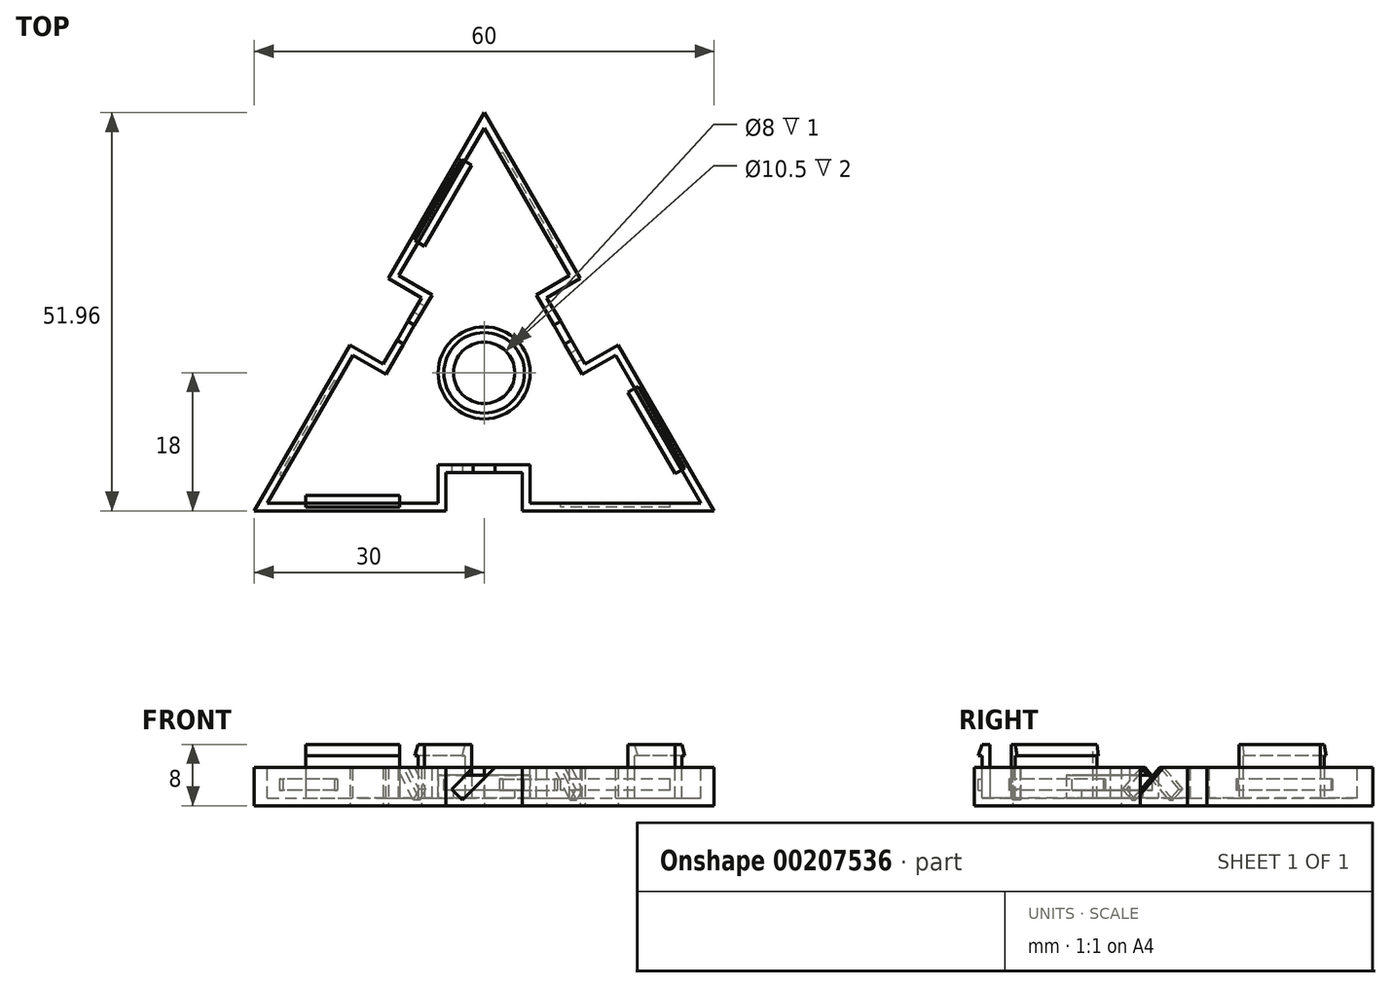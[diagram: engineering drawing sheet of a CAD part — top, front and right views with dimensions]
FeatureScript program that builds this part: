
annotation { "Feature Type Name" : "Feature", "Feature Type Description" : "" }
export const myFeature = defineFeature(function(context is Context, id is Id, definition is map)
    precondition{}
    {
        {
            var Q0;
            Q0=qCreatedBy(makeId("Top.planeOp"),FACE);
            var sketch = newSketch(context, id + "F0", { "sketchPlane" : qUnion([Q0])});
            skLineSegment(sketch, "E0", {"start": v(0, 0) * mm, "end": v(60, 0) * mm});
            skLineSegment(sketch, "E1", {"start": v(0, 0) * mm, "end": v(30, 51.96) * mm});
            skLineSegment(sketch, "E2", {"start": v(30, 51.96) * mm, "end": v(60, 0) * mm});
            skSolve(sketch);
        }
        {
            var Q0;
            Q0=makeQuery(id+"F0.imprint","IMPRINT",FACE,{"disambiguationData":[TD([[makeQuery(id+"F0.imprint","IMPRINT",EDGE,{"derivedFrom":sQuery(id+"F0.wireOp",EDGE,"E0")}),1.0]])]});
            extrude(context, id + "F1", {"entities" : qUnion([Q0]), "depth" : 10 * mm});
        }
        {
            var Q0;
            Q0=makeQuery(id+"F1.opExtrude","SWEPT_FACE",FACE,{"disambiguationData":[OSD([sQuery(id+"F0.wireOp",EDGE,"E0")])]});
            var sketch = newSketch(context, id + "F2", { "sketchPlane" : qUnion([Q0])});
            skLineSegment(sketch, "E3.bottom", {"start": v(25, 10) * mm, "end": v(35, 10) * mm});
            skLineSegment(sketch, "E3.top", {"start": v(25, 0) * mm, "end": v(35, 0) * mm});
            skLineSegment(sketch, "E3.left", {"start": v(25, 10) * mm, "end": v(25, 0) * mm});
            skLineSegment(sketch, "E3.right", {"start": v(35, 10) * mm, "end": v(35, 0) * mm});
            skSolve(sketch);
        }
        {
            var Q0;
            Q0=makeQuery(id+"F2.imprint","IMPRINT",FACE,{"disambiguationData":[TD([[makeQuery(id+"F2.imprint","IMPRINT",EDGE,{"derivedFrom":sQuery(id+"F2.wireOp",EDGE,"E3.bottom")}),-1.0]])]});
            extrude(context, id + "F3", {"entities" : qUnion([Q0]), "operationType" : NewBodyOperationType.REMOVE, "oppositeDirection" : true, "depth" : 5 * mm});
        }
        {
            var Q0;
            Q0=makeQuery(id+"F1.opExtrude","SWEPT_FACE",FACE,{"disambiguationData":[OSD([sQuery(id+"F0.wireOp",EDGE,"E1")])]});
            var sketch = newSketch(context, id + "F4", { "sketchPlane" : qUnion([Q0])});
            skLineSegment(sketch, "E4.bottom", {"start": v(-35, 10) * mm, "end": v(-25, 10) * mm});
            skLineSegment(sketch, "E4.top", {"start": v(-35, 0) * mm, "end": v(-25, 0) * mm});
            skLineSegment(sketch, "E4.left", {"start": v(-35, 10) * mm, "end": v(-35, 0) * mm});
            skLineSegment(sketch, "E4.right", {"start": v(-25, 10) * mm, "end": v(-25, 0) * mm});
            skSolve(sketch);
        }
        {
            var Q0;
            Q0=makeQuery(id+"F4.imprint","IMPRINT",FACE,{"disambiguationData":[TD([[makeQuery(id+"F4.imprint","IMPRINT",EDGE,{"derivedFrom":sQuery(id+"F4.wireOp",EDGE,"E4.bottom")}),1.0]])]});
            extrude(context, id + "F5", {"entities" : qUnion([Q0]), "operationType" : NewBodyOperationType.REMOVE, "oppositeDirection" : true, "depth" : 5 * mm});
        }
        {
            var Q0;
            Q0=makeQuery(id+"F1.opExtrude","SWEPT_FACE",FACE,{"disambiguationData":[OSD([sQuery(id+"F0.wireOp",EDGE,"E2")])]});
            var sketch = newSketch(context, id + "F6", { "sketchPlane" : qUnion([Q0])});
            skLineSegment(sketch, "E5.bottom", {"start": v(-5, 10) * mm, "end": v(5, 10) * mm});
            skLineSegment(sketch, "E5.top", {"start": v(-5, 0) * mm, "end": v(5, 0) * mm});
            skLineSegment(sketch, "E5.left", {"start": v(-5, 10) * mm, "end": v(-5, 0) * mm});
            skLineSegment(sketch, "E5.right", {"start": v(5, 10) * mm, "end": v(5, 0) * mm});
            skSolve(sketch);
        }
        {
            var Q0;
            Q0=makeQuery(id+"F6.imprint","IMPRINT",FACE,{"disambiguationData":[TD([[makeQuery(id+"F6.imprint","IMPRINT",EDGE,{"derivedFrom":sQuery(id+"F6.wireOp",EDGE,"E5.bottom")}),1.0]])]});
            extrude(context, id + "F7", {"entities" : qUnion([Q0]), "operationType" : NewBodyOperationType.REMOVE, "oppositeDirection" : true, "depth" : 5 * mm});
        }
        {
            var Q0;
            Q0=makeQuery(id+"F1.opExtrude","CAP_FACE",FACE,{"disambiguationData":[OSD([sQuery(id+"F0.wireOp",EDGE,"E0"),sQuery(id+"F0.wireOp",EDGE,"E1"),sQuery(id+"F0.wireOp",EDGE,"E2")])],"isStart":false});
            var sketch = newSketch(context, id + "F8", { "sketchPlane" : qUnion([Q0])});
            skLineSegment(sketch, "E6.0", {"start": v(23.2, 28.18) * mm, "end": v(18.87, 30.68) * mm});
            skLineSegment(sketch, "E6.1", {"start": v(17.2, 17.78) * mm, "end": v(23.2, 28.18) * mm});
            skLineSegment(sketch, "E6.2", {"start": v(17.2, 17.78) * mm, "end": v(12.87, 20.28) * mm});
            skLineSegment(sketch, "E6.3", {"start": v(1.73, 1) * mm, "end": v(12.87, 20.28) * mm});
            skLineSegment(sketch, "E6.4", {"start": v(42.8, 17.78) * mm, "end": v(47.13, 20.28) * mm});
            skLineSegment(sketch, "E6.5", {"start": v(36.8, 28.18) * mm, "end": v(42.8, 17.78) * mm});
            skLineSegment(sketch, "E6.6", {"start": v(36.8, 28.18) * mm, "end": v(41.13, 30.68) * mm});
            skLineSegment(sketch, "E6.7", {"start": v(30, 49.96) * mm, "end": v(41.13, 30.68) * mm});
            skLineSegment(sketch, "E6.8", {"start": v(47.13, 20.28) * mm, "end": v(58.27, 1) * mm});
            skLineSegment(sketch, "E6.9", {"start": v(36, 1) * mm, "end": v(58.27, 1) * mm});
            skLineSegment(sketch, "E6.10", {"start": v(36, 6) * mm, "end": v(36, 1) * mm});
            skLineSegment(sketch, "E6.11", {"start": v(24, 6) * mm, "end": v(36, 6) * mm});
            skLineSegment(sketch, "E6.12", {"start": v(18.87, 30.68) * mm, "end": v(30, 49.96) * mm});
            skLineSegment(sketch, "E6.13", {"start": v(24, 6) * mm, "end": v(24, 1) * mm});
            skLineSegment(sketch, "E6.14", {"start": v(1.73, 1) * mm, "end": v(24, 1) * mm});
            skSolve(sketch);
        }
        {
            var Q0;
            Q0=makeQuery(id+"F8.imprint","IMPRINT",FACE,{"disambiguationData":[TD([[makeQuery(id+"F8.imprint","IMPRINT",EDGE,{"derivedFrom":sQuery(id+"F8.wireOp",EDGE,"E6.0")}),-1.0]])]});
            extrude(context, id + "F9", {"entities" : qUnion([Q0]), "operationType" : NewBodyOperationType.REMOVE, "oppositeDirection" : true, "depth" : 9 * mm});
        }
        {
            var Q0;
            Q0=makeQuery(id+"F1.opExtrude","CAP_FACE",FACE,{"disambiguationData":[OSD([sQuery(id+"F0.wireOp",EDGE,"E0"),sQuery(id+"F0.wireOp",EDGE,"E1"),sQuery(id+"F0.wireOp",EDGE,"E2")])],"isStart":false});
            extrude(context, id + "F10", {"entities" : qUnion([Q0]), "operationType" : NewBodyOperationType.REMOVE, "oppositeDirection" : true, "depth" : 5 * mm});
        }
        {
            var Q0;
            Q0=makeQuery(id+"F9.boolean.opBoolean","COPY",FACE,{"derivedFrom":makeQuery(id+"F9.opExtrude","SWEPT_FACE",FACE,{"disambiguationData":[OSD([sQuery(id+"F8.wireOp",EDGE,"E6.12")])]})});
            var sketch = newSketch(context, id + "F11", { "sketchPlane" : qUnion([Q0])});
            skLineSegment(sketch, "E7.bottom", {"start": v(41, 8) * mm, "end": v(53.27, 8) * mm});
            skLineSegment(sketch, "E7.top", {"start": v(41, 1) * mm, "end": v(53.27, 1) * mm});
            skLineSegment(sketch, "E7.left", {"start": v(41, 8) * mm, "end": v(41, 1) * mm});
            skLineSegment(sketch, "E7.right", {"start": v(53.27, 8) * mm, "end": v(53.27, 1) * mm});
            skSolve(sketch);
        }
        {
            var Q0;
            {var subQ0=sQuery(id+"F11.wireOp",EDGE,"E7.top");Q0=makeQuery(id+"F11.imprint","IMPRINT",FACE,{"disambiguationData":[TD([[makeQuery(id+"F11.imprint","IMPRINT",EDGE,{"derivedFrom":subQ0}),1.0]])]});}
            var Q1;
            {var subQ0=sQuery(id+"F11.wireOp",EDGE,"E7.bottom");Q1=makeQuery(id+"F11.imprint","IMPRINT",FACE,{"disambiguationData":[TD([[makeQuery(id+"F11.imprint","IMPRINT",EDGE,{"derivedFrom":subQ0}),-1.0]])]});}
            extrude(context, id + "F12", {"entities" : qUnion([Q0, Q1]), "operationType" : NewBodyOperationType.ADD, "depth" : 1 * mm});
        }
        {
            var Q0;
            Q0=makeQuery(id+"F9.boolean.opBoolean","COPY",FACE,{"derivedFrom":makeQuery(id+"F9.opExtrude","SWEPT_FACE",FACE,{"disambiguationData":[OSD([sQuery(id+"F8.wireOp",EDGE,"E6.14")])]})});
            var sketch = newSketch(context, id + "F13", { "sketchPlane" : qUnion([Q0])});
            skLineSegment(sketch, "E8.bottom", {"start": v(-19, 8) * mm, "end": v(-6.73, 8) * mm});
            skLineSegment(sketch, "E8.top", {"start": v(-19, 1) * mm, "end": v(-6.73, 1) * mm});
            skLineSegment(sketch, "E8.left", {"start": v(-19, 8) * mm, "end": v(-19, 1) * mm});
            skLineSegment(sketch, "E8.right", {"start": v(-6.73, 8) * mm, "end": v(-6.73, 1) * mm});
            skSolve(sketch);
        }
        {
            var Q0;
            {var subQ0=sQuery(id+"F13.wireOp",EDGE,"E8.top");Q0=makeQuery(id+"F13.imprint","IMPRINT",FACE,{"disambiguationData":[TD([[makeQuery(id+"F13.imprint","IMPRINT",EDGE,{"derivedFrom":subQ0}),-1.0]])]});}
            var Q1;
            {var subQ0=sQuery(id+"F13.wireOp",EDGE,"E8.bottom");Q1=makeQuery(id+"F13.imprint","IMPRINT",FACE,{"disambiguationData":[TD([[makeQuery(id+"F13.imprint","IMPRINT",EDGE,{"derivedFrom":subQ0}),-1.0]])]});}
            extrude(context, id + "F14", {"entities" : qUnion([Q0, Q1]), "operationType" : NewBodyOperationType.ADD, "depth" : 1 * mm});
        }
        {
            var Q0;
            Q0=makeQuery(id+"F9.boolean.opBoolean","COPY",FACE,{"derivedFrom":makeQuery(id+"F9.opExtrude","SWEPT_FACE",FACE,{"disambiguationData":[OSD([sQuery(id+"F8.wireOp",EDGE,"E6.8")])]})});
            var sketch = newSketch(context, id + "F15", { "sketchPlane" : qUnion([Q0])});
            skLineSegment(sketch, "E9.bottom", {"start": v(11, 1) * mm, "end": v(23.27, 1) * mm});
            skLineSegment(sketch, "E9.top", {"start": v(11, 8) * mm, "end": v(23.27, 8) * mm});
            skLineSegment(sketch, "E9.left", {"start": v(11, 1) * mm, "end": v(11, 8) * mm});
            skLineSegment(sketch, "E9.right", {"start": v(23.27, 1) * mm, "end": v(23.27, 8) * mm});
            skSolve(sketch);
        }
        {
            var Q0;
            {var subQ0=sQuery(id+"F15.wireOp",EDGE,"E9.bottom");Q0=makeQuery(id+"F15.imprint","IMPRINT",FACE,{"disambiguationData":[TD([[makeQuery(id+"F15.imprint","IMPRINT",EDGE,{"derivedFrom":subQ0}),1.0]])]});}
            var Q1;
            {var subQ0=sQuery(id+"F15.wireOp",EDGE,"E9.top");Q1=makeQuery(id+"F15.imprint","IMPRINT",FACE,{"disambiguationData":[TD([[makeQuery(id+"F15.imprint","IMPRINT",EDGE,{"derivedFrom":subQ0}),-1.0]])]});}
            extrude(context, id + "F16", {"entities" : qUnion([Q0, Q1]), "operationType" : NewBodyOperationType.ADD, "depth" : 1 * mm});
        }
        {
            var Q0;
            Q0=makeQuery(id+"F14.opExtrude","CAP_FACE",FACE,{"disambiguationData":[OSD([sQuery(id+"F13.wireOp",EDGE,"E8.bottom"),sQuery(id+"F13.wireOp",EDGE,"E8.top"),sQuery(id+"F13.wireOp",EDGE,"E8.left"),sQuery(id+"F13.wireOp",EDGE,"E8.right")])],"isStart":true});
            var sketch = newSketch(context, id + "F17", { "sketchPlane" : qUnion([Q0])});
            skLineSegment(sketch, "E10.bottom", {"start": v(6.73, 8) * mm, "end": v(19, 8) * mm});
            skLineSegment(sketch, "E10.top", {"start": v(6.73, 6.5) * mm, "end": v(19, 6.5) * mm});
            skLineSegment(sketch, "E10.left", {"start": v(6.73, 8) * mm, "end": v(6.73, 6.5) * mm});
            skLineSegment(sketch, "E10.right", {"start": v(19, 8) * mm, "end": v(19, 6.5) * mm});
            skSolve(sketch);
        }
        {
            var Q0;
            Q0=makeQuery(id+"F17.imprint","IMPRINT",FACE,{"disambiguationData":[TD([[makeQuery(id+"F17.imprint","IMPRINT",EDGE,{"derivedFrom":sQuery(id+"F17.wireOp",EDGE,"E10.bottom")}),1.0]])]});
            extrude(context, id + "F18", {"entities" : qUnion([Q0]), "operationType" : NewBodyOperationType.ADD, "depth" : 0.5 * mm});
        }
        {
            var Q0;
            Q0=makeQuery(id+"F18.opExtrude","CAP_EDGE",EDGE,{"disambiguationData":[OSD([sQuery(id+"F17.wireOp",EDGE,"E10.bottom")])],"isStart":false});
            chamfer(context, id + "F19", {"entities" : qUnion([Q0]), "chamferType" : ChamferType.TWO_OFFSETS, "width1" : 0.5 * mm, "oppositeDirection" : true, "width2" : 1.5 * mm, "tangentPropagation" : true});
        }
        {
            var Q0;
            Q0=makeQuery(id+"F16.opExtrude","CAP_FACE",FACE,{"disambiguationData":[OSD([sQuery(id+"F15.wireOp",EDGE,"E9.bottom"),sQuery(id+"F15.wireOp",EDGE,"E9.top"),sQuery(id+"F15.wireOp",EDGE,"E9.left"),sQuery(id+"F15.wireOp",EDGE,"E9.right")])],"isStart":true});
            var sketch = newSketch(context, id + "F20", { "sketchPlane" : qUnion([Q0])});
            skLineSegment(sketch, "E11.bottom", {"start": v(-23.27, 8) * mm, "end": v(-11, 8) * mm});
            skLineSegment(sketch, "E11.top", {"start": v(-23.27, 6.5) * mm, "end": v(-11, 6.5) * mm});
            skLineSegment(sketch, "E11.left", {"start": v(-23.27, 8) * mm, "end": v(-23.27, 6.5) * mm});
            skLineSegment(sketch, "E11.right", {"start": v(-11, 8) * mm, "end": v(-11, 6.5) * mm});
            skSolve(sketch);
        }
        {
            var Q0;
            Q0=makeQuery(id+"F20.imprint","IMPRINT",FACE,{"disambiguationData":[TD([[makeQuery(id+"F20.imprint","IMPRINT",EDGE,{"derivedFrom":sQuery(id+"F20.wireOp",EDGE,"E11.bottom")}),1.0]])]});
            extrude(context, id + "F21", {"entities" : qUnion([Q0]), "operationType" : NewBodyOperationType.ADD, "depth" : 0.5 * mm});
        }
        {
            var Q0;
            Q0=makeQuery(id+"F21.opExtrude","CAP_EDGE",EDGE,{"disambiguationData":[OSD([sQuery(id+"F20.wireOp",EDGE,"E11.bottom")])],"isStart":false});
            chamfer(context, id + "F22", {"entities" : qUnion([Q0]), "chamferType" : ChamferType.TWO_OFFSETS, "width1" : 0.5 * mm, "oppositeDirection" : true, "width2" : 1.5 * mm, "tangentPropagation" : true});
        }
        {
            var Q0;
            Q0=makeQuery(id+"F12.opExtrude","CAP_FACE",FACE,{"disambiguationData":[OSD([sQuery(id+"F11.wireOp",EDGE,"E7.bottom"),sQuery(id+"F11.wireOp",EDGE,"E7.top"),sQuery(id+"F11.wireOp",EDGE,"E7.left"),sQuery(id+"F11.wireOp",EDGE,"E7.right")])],"isStart":true});
            var sketch = newSketch(context, id + "F23", { "sketchPlane" : qUnion([Q0])});
            skLineSegment(sketch, "E12.bottom", {"start": v(-53.27, 8) * mm, "end": v(-41, 8) * mm});
            skLineSegment(sketch, "E12.top", {"start": v(-53.27, 6.5) * mm, "end": v(-41, 6.5) * mm});
            skLineSegment(sketch, "E12.left", {"start": v(-53.27, 8) * mm, "end": v(-53.27, 6.5) * mm});
            skLineSegment(sketch, "E12.right", {"start": v(-41, 8) * mm, "end": v(-41, 6.5) * mm});
            skSolve(sketch);
        }
        {
            var Q0;
            Q0=makeQuery(id+"F23.imprint","IMPRINT",FACE,{"disambiguationData":[TD([[makeQuery(id+"F23.imprint","IMPRINT",EDGE,{"derivedFrom":sQuery(id+"F23.wireOp",EDGE,"E12.bottom")}),1.0]])]});
            extrude(context, id + "F24", {"entities" : qUnion([Q0]), "operationType" : NewBodyOperationType.ADD, "depth" : 0.5 * mm});
        }
        {
            var Q0;
            Q0=makeQuery(id+"F24.opExtrude","CAP_EDGE",EDGE,{"disambiguationData":[OSD([sQuery(id+"F23.wireOp",EDGE,"E12.bottom")])],"isStart":false});
            chamfer(context, id + "F25", {"entities" : qUnion([Q0]), "chamferType" : ChamferType.TWO_OFFSETS, "width1" : 0.5 * mm, "oppositeDirection" : true, "width2" : 1.5 * mm, "tangentPropagation" : true});
        }
        {
            var Q0;
            Q0=makeQuery(id+"F9.boolean.opBoolean","COPY",FACE,{"derivedFrom":makeQuery(id+"F9.opExtrude","SWEPT_FACE",FACE,{"disambiguationData":[OSD([sQuery(id+"F8.wireOp",EDGE,"E6.7")])]})});
            var sketch = newSketch(context, id + "F26", { "sketchPlane" : qUnion([Q0])});
            skLineSegment(sketch, "E13.bottom", {"start": v(-24.27, 3.5) * mm, "end": v(-10, 3.5) * mm});
            skLineSegment(sketch, "E13.top", {"start": v(-24.27, 2) * mm, "end": v(-10, 2) * mm});
            skLineSegment(sketch, "E13.left", {"start": v(-24.27, 3.5) * mm, "end": v(-24.27, 2) * mm});
            skLineSegment(sketch, "E13.right", {"start": v(-10, 3.5) * mm, "end": v(-10, 2) * mm});
            skSolve(sketch);
        }
        {
            var Q0;
            Q0=makeQuery(id+"F26.imprint","IMPRINT",FACE,{"disambiguationData":[TD([[makeQuery(id+"F26.imprint","IMPRINT",EDGE,{"derivedFrom":sQuery(id+"F26.wireOp",EDGE,"E13.bottom")}),-1.0]])]});
            extrude(context, id + "F27", {"entities" : qUnion([Q0]), "operationType" : NewBodyOperationType.REMOVE, "oppositeDirection" : true, "depth" : 0.5 * mm});
        }
        {
            var Q0;
            Q0=makeQuery(id+"F9.boolean.opBoolean","COPY",FACE,{"derivedFrom":makeQuery(id+"F9.opExtrude","SWEPT_FACE",FACE,{"disambiguationData":[OSD([sQuery(id+"F8.wireOp",EDGE,"E6.9")])]})});
            var sketch = newSketch(context, id + "F28", { "sketchPlane" : qUnion([Q0])});
            skLineSegment(sketch, "E14.bottom", {"start": v(-54.27, 2) * mm, "end": v(-40, 2) * mm});
            skLineSegment(sketch, "E14.top", {"start": v(-54.27, 3.5) * mm, "end": v(-40, 3.5) * mm});
            skLineSegment(sketch, "E14.left", {"start": v(-54.27, 2) * mm, "end": v(-54.27, 3.5) * mm});
            skLineSegment(sketch, "E14.right", {"start": v(-40, 2) * mm, "end": v(-40, 3.5) * mm});
            skSolve(sketch);
        }
        {
            var Q0;
            Q0=makeQuery(id+"F28.imprint","IMPRINT",FACE,{"disambiguationData":[TD([[makeQuery(id+"F28.imprint","IMPRINT",EDGE,{"derivedFrom":sQuery(id+"F28.wireOp",EDGE,"E14.bottom")}),1.0]])]});
            extrude(context, id + "F29", {"entities" : qUnion([Q0]), "operationType" : NewBodyOperationType.REMOVE, "oppositeDirection" : true, "depth" : 0.5 * mm});
        }
        {
            var Q0;
            Q0=makeQuery(id+"F9.boolean.opBoolean","COPY",FACE,{"derivedFrom":makeQuery(id+"F9.opExtrude","SWEPT_FACE",FACE,{"disambiguationData":[OSD([sQuery(id+"F8.wireOp",EDGE,"E6.3")])]})});
            var sketch = newSketch(context, id + "F30", { "sketchPlane" : qUnion([Q0])});
            skLineSegment(sketch, "E15.bottom", {"start": v(20, 3.5) * mm, "end": v(5.73, 3.5) * mm});
            skLineSegment(sketch, "E15.top", {"start": v(20, 2) * mm, "end": v(5.73, 2) * mm});
            skLineSegment(sketch, "E15.left", {"start": v(5.73, 3.5) * mm, "end": v(5.73, 2) * mm});
            skLineSegment(sketch, "E15.right", {"start": v(20, 3.5) * mm, "end": v(20, 2) * mm});
            skSolve(sketch);
        }
        {
            var Q0;
            Q0=makeQuery(id+"F30.imprint","IMPRINT",FACE,{"disambiguationData":[TD([[makeQuery(id+"F30.imprint","IMPRINT",EDGE,{"derivedFrom":sQuery(id+"F30.wireOp",EDGE,"E15.bottom")}),1.0]])]});
            extrude(context, id + "F31", {"entities" : qUnion([Q0]), "operationType" : NewBodyOperationType.REMOVE, "oppositeDirection" : true, "depth" : 0.5 * mm});
        }
        {
            var Q0;
            Q0=makeQuery(id+"F9.boolean.opBoolean","COPY",FACE,{"derivedFrom":makeQuery(id+"F9.opExtrude","CAP_FACE",FACE,{"disambiguationData":[OSD([sQuery(id+"F8.wireOp",EDGE,"E6.0"),sQuery(id+"F8.wireOp",EDGE,"E6.1"),sQuery(id+"F8.wireOp",EDGE,"E6.2"),sQuery(id+"F8.wireOp",EDGE,"E6.3"),sQuery(id+"F8.wireOp",EDGE,"E6.4"),sQuery(id+"F8.wireOp",EDGE,"E6.5"),sQuery(id+"F8.wireOp",EDGE,"E6.6"),sQuery(id+"F8.wireOp",EDGE,"E6.7"),sQuery(id+"F8.wireOp",EDGE,"E6.8"),sQuery(id+"F8.wireOp",EDGE,"E6.9"),sQuery(id+"F8.wireOp",EDGE,"E6.10"),sQuery(id+"F8.wireOp",EDGE,"E6.11"),sQuery(id+"F8.wireOp",EDGE,"E6.12"),sQuery(id+"F8.wireOp",EDGE,"E6.13"),sQuery(id+"F8.wireOp",EDGE,"E6.14")])],"isStart":false})});
            var sketch = newSketch(context, id + "F32", { "sketchPlane" : qUnion([Q0])});
            skCircle(sketch, "E16", {"center": v(30, 18) * mm, "radius": 6 * mm});
            skSolve(sketch);
        }
        {
            var Q0;
            Q0=makeQuery(id+"F32.imprint","IMPRINT",FACE,{"disambiguationData":[TD([[makeQuery(id+"F32.imprint","IMPRINT",EDGE,{"derivedFrom":sQuery(id+"F32.wireOp",EDGE,"E16")}),1.0]])]});
            extrude(context, id + "F33", {"entities" : qUnion([Q0]), "operationType" : NewBodyOperationType.ADD, "depth" : 4 * mm});
        }
        {
            var Q0;
            Q0=makeQuery(id+"F33.opExtrude","CAP_FACE",FACE,{"disambiguationData":[OSD([sQuery(id+"F32.wireOp",EDGE,"E16")])],"isStart":false});
            var sketch = newSketch(context, id + "F34", { "sketchPlane" : qUnion([Q0])});
            skCircle(sketch, "E17", {"center": v(30, 18) * mm, "radius": 5.25 * mm});
            skSolve(sketch);
        }
        {
            var Q0;
            Q0=makeQuery(id+"F34.imprint","IMPRINT",FACE,{"disambiguationData":[TD([[makeQuery(id+"F34.imprint","IMPRINT",EDGE,{"derivedFrom":sQuery(id+"F34.wireOp",EDGE,"E17")}),1.0]])]});
            extrude(context, id + "F35", {"entities" : qUnion([Q0]), "operationType" : NewBodyOperationType.REMOVE, "oppositeDirection" : true, "depth" : 3 * mm});
        }
        {
            var Q0;
            Q0=makeQuery(id+"F35.boolean.opBoolean","COPY",FACE,{"derivedFrom":makeQuery(id+"F35.opExtrude","CAP_FACE",FACE,{"disambiguationData":[OSD([sQuery(id+"F34.wireOp",EDGE,"E17")])],"isStart":false})});
            var sketch = newSketch(context, id + "F36", { "sketchPlane" : qUnion([Q0])});
            skCircle(sketch, "E18", {"center": v(30, 18) * mm, "radius": 4 * mm});
            skSolve(sketch);
        }
        {
            var Q0;
            Q0=makeQuery(id+"F36.imprint","IMPRINT",FACE,{"disambiguationData":[TD([[makeQuery(id+"F36.imprint","IMPRINT",EDGE,{"derivedFrom":sQuery(id+"F36.wireOp",EDGE,"E18")}),1.0]])]});
            extrude(context, id + "F37", {"entities" : qUnion([Q0]), "operationType" : NewBodyOperationType.REMOVE, "oppositeDirection" : true, "depth" : 1 * mm});
        }
        {
            var Q0;
            Q0=makeQuery(id+"F3.boolean.opBoolean","COPY",FACE,{"derivedFrom":makeQuery(id+"F3.opExtrude","CAP_FACE",FACE,{"disambiguationData":[OSD([sQuery(id+"F2.wireOp",EDGE,"E3.bottom"),sQuery(id+"F2.wireOp",EDGE,"E3.top"),sQuery(id+"F2.wireOp",EDGE,"E3.left"),sQuery(id+"F2.wireOp",EDGE,"E3.right")])],"isStart":false})});
            var sketch = newSketch(context, id + "F38", { "sketchPlane" : qUnion([Q0])});
            skLineSegment(sketch, "E19", {"start": v(27.17, 0.76) * mm, "end": v(34.24, 7.83) * mm});
            skLineSegment(sketch, "E20", {"start": v(34.24, 7.83) * mm, "end": v(32.83, 9.24) * mm});
            skLineSegment(sketch, "E21", {"start": v(32.83, 9.24) * mm, "end": v(25.76, 2.17) * mm});
            skLineSegment(sketch, "E22", {"start": v(25.76, 2.17) * mm, "end": v(27.17, 0.76) * mm});
            skLineSegment(sketch, "E23", {"start": v(32.83, 9.24) * mm, "end": v(27.17, 0.76) * mm, "construction": true});
            skLineSegment(sketch, "E24", {"start": v(25.76, 2.17) * mm, "end": v(34.24, 7.83) * mm, "construction": true});
            skPoint(sketch, "E25", {"position": v(30, 5) * mm});
            skSolve(sketch);
        }
        {
            var Q0;
            {var subQ0=sQuery(id+"F38.wireOp",EDGE,"E22");Q0=makeQuery(id+"F38.imprint","IMPRINT",FACE,{"disambiguationData":[TD([[makeQuery(id+"F38.imprint","IMPRINT",EDGE,{"derivedFrom":subQ0}),1.0]])]});}
            extrude(context, id + "F39", {"entities" : qUnion([Q0]), "operationType" : NewBodyOperationType.REMOVE, "oppositeDirection" : true, "depth" : 1 * mm});
        }
        {
            var Q0;
            Q0=makeQuery(id+"F7.boolean.opBoolean","COPY",FACE,{"derivedFrom":makeQuery(id+"F7.opExtrude","CAP_FACE",FACE,{"disambiguationData":[OSD([sQuery(id+"F6.wireOp",EDGE,"E5.bottom"),sQuery(id+"F6.wireOp",EDGE,"E5.top"),sQuery(id+"F6.wireOp",EDGE,"E5.left"),sQuery(id+"F6.wireOp",EDGE,"E5.right")])],"isStart":false})});
            var sketch = newSketch(context, id + "F40", { "sketchPlane" : qUnion([Q0])});
            skLineSegment(sketch, "E26", {"start": v(-2.83, 0.76) * mm, "end": v(4.24, 7.83) * mm});
            skLineSegment(sketch, "E27", {"start": v(4.24, 7.83) * mm, "end": v(2.83, 9.24) * mm});
            skLineSegment(sketch, "E28", {"start": v(2.83, 9.24) * mm, "end": v(-4.24, 2.17) * mm});
            skLineSegment(sketch, "E29", {"start": v(-4.24, 2.17) * mm, "end": v(-2.83, 0.76) * mm});
            skLineSegment(sketch, "E30", {"start": v(2.83, 9.24) * mm, "end": v(-2.83, 0.76) * mm, "construction": true});
            skLineSegment(sketch, "E31", {"start": v(-4.24, 2.17) * mm, "end": v(4.24, 7.83) * mm, "construction": true});
            skPoint(sketch, "E32", {"position": v(0, 5) * mm});
            skSolve(sketch);
        }
        {
            var Q0;
            {var subQ0=sQuery(id+"F40.wireOp",EDGE,"E29");Q0=makeQuery(id+"F40.imprint","IMPRINT",FACE,{"disambiguationData":[TD([[makeQuery(id+"F40.imprint","IMPRINT",EDGE,{"derivedFrom":subQ0}),1.0]])]});}
            extrude(context, id + "F41", {"entities" : qUnion([Q0]), "operationType" : NewBodyOperationType.REMOVE, "oppositeDirection" : true, "depth" : 1 * mm});
        }
        {
            var Q0;
            Q0=makeQuery(id+"F5.boolean.opBoolean","COPY",FACE,{"derivedFrom":makeQuery(id+"F5.opExtrude","CAP_FACE",FACE,{"disambiguationData":[OSD([sQuery(id+"F4.wireOp",EDGE,"E4.bottom"),sQuery(id+"F4.wireOp",EDGE,"E4.top"),sQuery(id+"F4.wireOp",EDGE,"E4.left"),sQuery(id+"F4.wireOp",EDGE,"E4.right")])],"isStart":false})});
            var sketch = newSketch(context, id + "F42", { "sketchPlane" : qUnion([Q0])});
            skLineSegment(sketch, "E33", {"start": v(-32.83, 0.76) * mm, "end": v(-25.76, 7.83) * mm});
            skLineSegment(sketch, "E34", {"start": v(-25.76, 7.83) * mm, "end": v(-27.17, 9.24) * mm});
            skLineSegment(sketch, "E35", {"start": v(-27.17, 9.24) * mm, "end": v(-34.24, 2.17) * mm});
            skLineSegment(sketch, "E36", {"start": v(-34.24, 2.17) * mm, "end": v(-32.83, 0.76) * mm});
            skLineSegment(sketch, "E37", {"start": v(-27.17, 9.24) * mm, "end": v(-32.83, 0.76) * mm, "construction": true});
            skLineSegment(sketch, "E38", {"start": v(-34.24, 2.17) * mm, "end": v(-25.76, 7.83) * mm, "construction": true});
            skPoint(sketch, "E39", {"position": v(-30, 5) * mm});
            skSolve(sketch);
        }
        {
            var Q0;
            {var subQ0=sQuery(id+"F42.wireOp",EDGE,"E36");Q0=makeQuery(id+"F42.imprint","IMPRINT",FACE,{"disambiguationData":[TD([[makeQuery(id+"F42.imprint","IMPRINT",EDGE,{"derivedFrom":subQ0}),1.0]])]});}
            extrude(context, id + "F43", {"entities" : qUnion([Q0]), "operationType" : NewBodyOperationType.REMOVE, "oppositeDirection" : true, "depth" : 1 * mm});
        }
        {
            var Q0;
            Q0=makeQuery(id+"F33.opExtrude","CAP_FACE",FACE,{"disambiguationData":[OSD([sQuery(id+"F32.wireOp",EDGE,"E16")])],"isStart":false});
            extrude(context, id + "F44", {"entities" : qUnion([Q0]), "operationType" : NewBodyOperationType.REMOVE, "oppositeDirection" : true, "depth" : 1 * mm});
        }
    });
